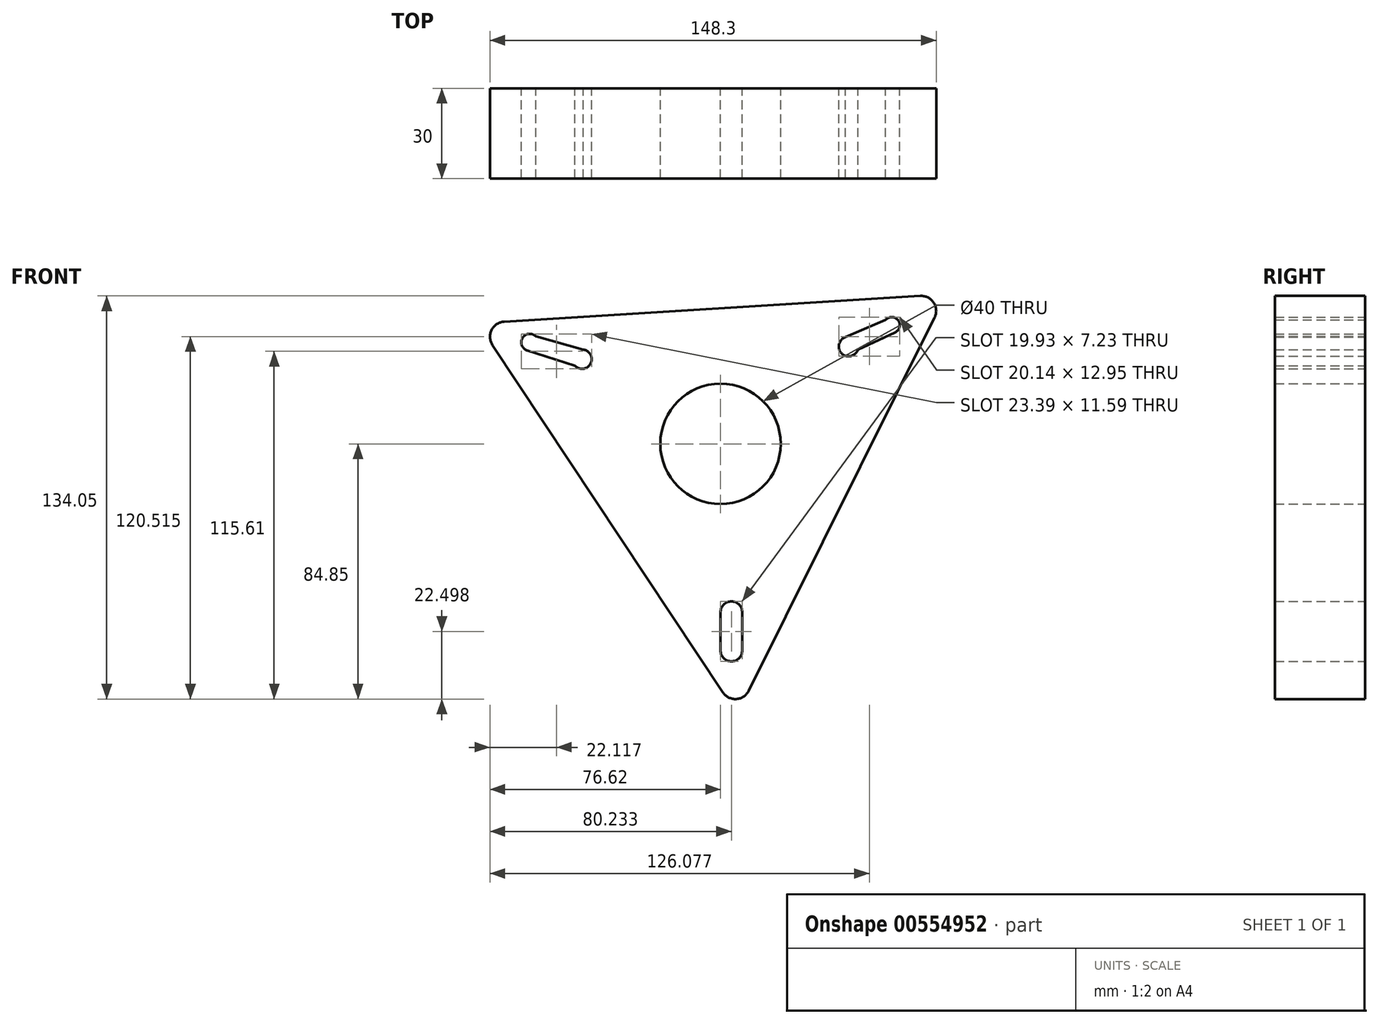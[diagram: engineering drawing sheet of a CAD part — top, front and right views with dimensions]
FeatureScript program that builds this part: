
annotation { "Feature Type Name" : "Feature", "Feature Type Description" : "" }
export const myFeature = defineFeature(function(context is Context, id is Id, definition is map)
    precondition{}
    {
        {
            var Q0;
            Q0=qCreatedBy(makeId("Front.planeOp"),FACE);
            var sketch = newSketch(context, id + "F0", { "sketchPlane" : qUnion([Q0])});
            skCircle(sketch, "E0", {"center": v(0, 0) * mm, "radius": 20 * mm});
            skCircle(sketch, "E1.cCircle", {"center": v(0, 0) * mm, "radius": 45 * mm, "construction": true});
            skLineSegment(sketch, "E1.0", {"start": v(71.16, 41.97) * mm, "end": v(9.41, -82.08) * mm});
            skLineSegment(sketch, "E1.1", {"start": v(0.77, -82.6) * mm, "end": v(-75.79, 32.88) * mm});
            skLineSegment(sketch, "E1.2", {"start": v(-71.93, 40.64) * mm, "end": v(66.37, 49.2) * mm});
            skPoint(sketch, "E1.0.midPoint", {"position": v(40.29, -20.05) * mm});
            skPoint(sketch, "E2.center.orphan", {"position": v(5, 0) * mm});
            skPoint(sketch, "E3.visualSharp", {"position": v(-80.57, 40.1) * mm});
            skArc(sketch, "E3.filletArc", {"start": v(-71.93, 40.64) * mm, "mid": v(-76.1, 37.88) * mm, "end": v(-75.79, 32.88) * mm});
            skPoint(sketch, "E4.visualSharp", {"position": v(75.02, 49.73) * mm});
            skArc(sketch, "E4.filletArc", {"start": v(71.16, 41.97) * mm, "mid": v(70.85, 46.96) * mm, "end": v(66.37, 49.2) * mm});
            skPoint(sketch, "E5.visualSharp", {"position": v(5.56, -89.83) * mm});
            skArc(sketch, "E5.filletArc", {"start": v(0.77, -82.6) * mm, "mid": v(5.25, -84.84) * mm, "end": v(9.41, -82.08) * mm});
            skLineSegment(sketch, "E6", {"start": v(41.52, 35.46) * mm, "end": v(54.86, 41.17) * mm});
            skLineSegment(sketch, "E7", {"start": v(58.04, 37.04) * mm, "end": v(45.65, 31.33) * mm});
            skArc(sketch, "E8", {"start": v(58.04, 37.04) * mm, "mid": v(59.03, 41.1) * mm, "end": v(54.86, 41.17) * mm});
            skArc(sketch, "E9", {"start": v(41.52, 35.46) * mm, "mid": v(40.25, 30.06) * mm, "end": v(45.65, 31.33) * mm});
            skLineSegment(sketch, "E10", {"start": v(7.23, -56) * mm, "end": v(7.23, -68.7) * mm});
            skLineSegment(sketch, "E11", {"start": v(0, -56) * mm, "end": v(0, -68.7) * mm});
            skArc(sketch, "E12", {"start": v(7.23, -56) * mm, "mid": v(3.61, -52.39) * mm, "end": v(0, -56) * mm});
            skArc(sketch, "E13", {"start": v(0, -68.7) * mm, "mid": v(3.61, -72.32) * mm, "end": v(7.23, -68.7) * mm});
            skPoint(sketch, "E14.MirrorCS.end.orphan", {"position": v(-54.86, 41.17) * mm});
            skPoint(sketch, "E14.MirrorCS.start.orphan", {"position": v(-41.52, 35.46) * mm});
            skPoint(sketch, "E15.MirrorCS.end.orphan", {"position": v(-45.65, 31.33) * mm});
            skPoint(sketch, "E15.MirrorCS.start.orphan", {"position": v(-58.04, 37.04) * mm});
            skLineSegment(sketch, "E16", {"start": v(-61.37, 35.77) * mm, "end": v(-45.65, 31.33) * mm});
            skLineSegment(sketch, "E17", {"start": v(-64.23, 31.01) * mm, "end": v(-48.35, 25.93) * mm});
            skArc(sketch, "E18", {"start": v(-48.35, 25.93) * mm, "mid": v(-43.15, 26.7) * mm, "end": v(-45.65, 31.33) * mm});
            skArc(sketch, "E19", {"start": v(-61.37, 35.77) * mm, "mid": v(-65.8, 35.2) * mm, "end": v(-64.23, 31.01) * mm});
            skLineSegment(sketch, "E20", {"start": v(0, 0) * mm, "end": v(0, 45) * mm});
            skLineSegment(sketch, "E21", {"start": v(0, 0) * mm, "end": v(40.29, -20.05) * mm});
            skLineSegment(sketch, "E22", {"start": v(0, 0) * mm, "end": v(-37.5, -24.86) * mm});
            skSolve(sketch);
        }
        {
            var Q0;
            Q0 = qSketchRegion(id + "F0", true);
            extrude(context, id + "F1", {"entities" : qUnion([Q0]), "depth" : 30 * mm, "offsetDistance" : 25 * mm});
        }
    });
